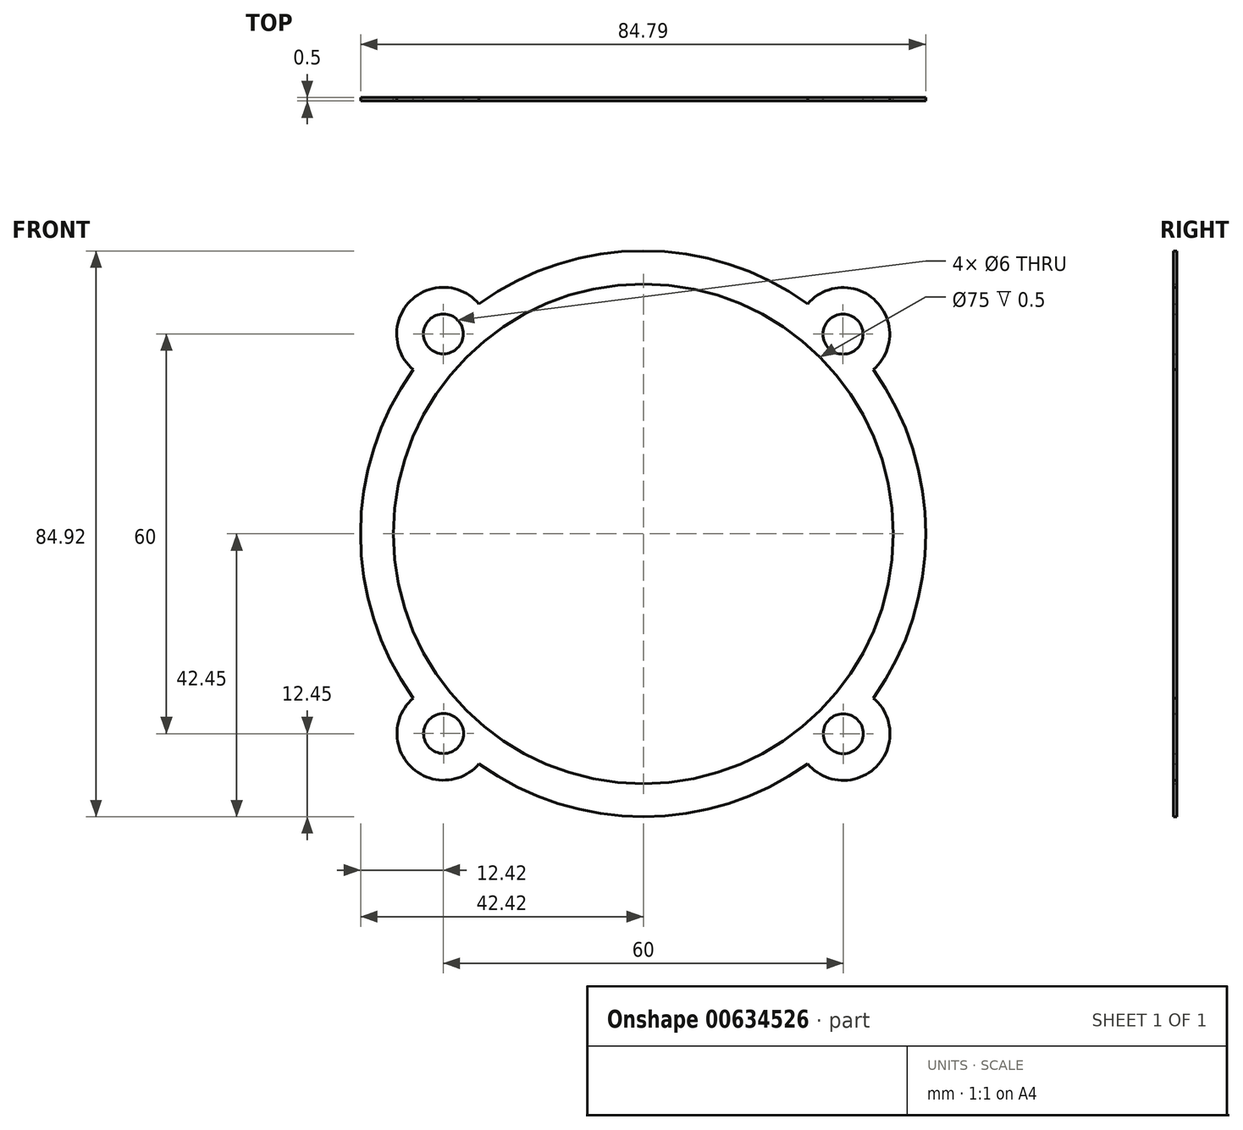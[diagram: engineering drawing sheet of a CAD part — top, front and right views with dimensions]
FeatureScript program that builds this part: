
annotation { "Feature Type Name" : "Feature", "Feature Type Description" : "" }
export const myFeature = defineFeature(function(context is Context, id is Id, definition is map)
    precondition{}
    {
        {
            var Q0;
            Q0=qCreatedBy(makeId("Front.planeOp"),FACE);
            var sketch = newSketch(context, id + "F0", { "sketchPlane" : qUnion([Q0])});
            skPoint(sketch, "E0.middle", {"position": v(0, 0) * mm});
            skCircle(sketch, "E1", {"center": v(-30, 30) * mm, "radius": 3 * mm});
            skCircle(sketch, "E2", {"center": v(29.96, 29.97) * mm, "radius": 3 * mm});
            skCircle(sketch, "E3", {"center": v(30, -30) * mm, "radius": 3 * mm});
            skCircle(sketch, "E4", {"center": v(-29.96, -29.97) * mm, "radius": 3 * mm});
            skCircle(sketch, "E5", {"center": v(0, 0) * mm, "radius": 37.5 * mm});
            skArc(sketch, "E6", {"start": v(-24.66, 34.52) * mm, "mid": v(-34.95, 34.95) * mm, "end": v(-34.52, 24.66) * mm});
            skArc(sketch, "E7", {"start": v(-34.52, -24.66) * mm, "mid": v(-34.91, -34.92) * mm, "end": v(-24.65, -34.53) * mm});
            skArc(sketch, "E8", {"start": v(24.66, -34.52) * mm, "mid": v(34.95, -34.95) * mm, "end": v(34.52, -24.66) * mm});
            skArc(sketch, "E9", {"start": v(34.52, 24.66) * mm, "mid": v(34.91, 34.92) * mm, "end": v(24.65, 34.53) * mm});
            skArc(sketch, "E10", {"start": v(-34.52, 24.66) * mm, "mid": v(-42.42, 0) * mm, "end": v(-34.52, -24.66) * mm});
            skArc(sketch, "E11", {"start": v(-24.65, -34.53) * mm, "mid": v(0, -42.45) * mm, "end": v(24.66, -34.52) * mm});
            skArc(sketch, "E12", {"start": v(34.52, -24.66) * mm, "mid": v(42.37, 0) * mm, "end": v(34.52, 24.66) * mm});
            skArc(sketch, "E13", {"start": v(24.65, 34.53) * mm, "mid": v(0, 42.47) * mm, "end": v(-24.66, 34.52) * mm});
            skSolve(sketch);
        }
        {
            var Q0;
            Q0 = qSketchRegion(id + "F0", true);
            extrude(context, id + "F1", {"entities" : qUnion([Q0]), "depth" : 0.5 * mm, "offsetDistance" : 25 * mm});
        }
    });
